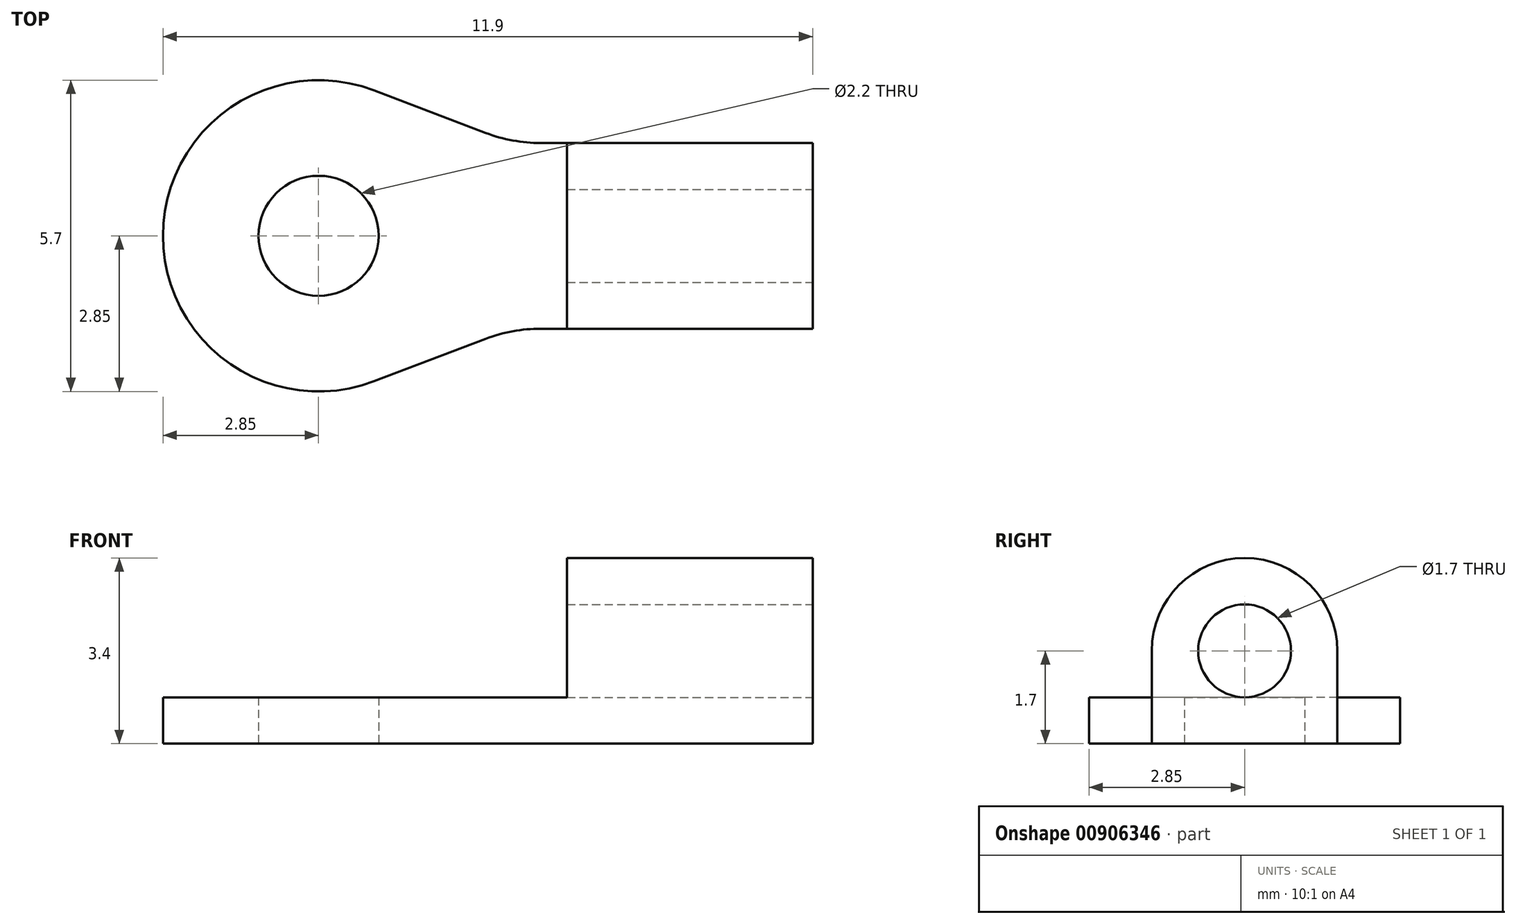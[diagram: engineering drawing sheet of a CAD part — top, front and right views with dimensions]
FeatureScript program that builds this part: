
annotation { "Feature Type Name" : "Feature", "Feature Type Description" : "" }
export const myFeature = defineFeature(function(context is Context, id is Id, definition is map)
    precondition{}
    {
        {
            var Q0;
            Q0=qCreatedBy(makeId("Top.planeOp"),FACE);
            var sketch = newSketch(context, id + "F0", { "sketchPlane" : qUnion([Q0])});
            skLineSegment(sketch, "E0.left", {"start": v(0, 2.85) * mm, "end": v(0, 2.85) * mm});
            skLineSegment(sketch, "E0.right", {"start": v(11.9, 1.15) * mm, "end": v(11.9, 4.55) * mm});
            skPoint(sketch, "E1.visualSharp", {"position": v(0, 5.7) * mm});
            skArc(sketch, "E1.filletArc", {"start": v(2.85, 5.7) * mm, "mid": v(0.83, 4.87) * mm, "end": v(0, 2.85) * mm});
            skPoint(sketch, "E2.visualSharp", {"position": v(0, 0) * mm});
            skArc(sketch, "E2.filletArc", {"start": v(0, 2.85) * mm, "mid": v(0.83, 0.83) * mm, "end": v(2.85, 0) * mm});
            skLineSegment(sketch, "E3.0", {"start": v(6.4, 1.1) * mm, "end": v(6.4, 1.15) * mm});
            skCircle(sketch, "E4", {"center": v(2.85, 2.85) * mm, "radius": 1.1 * mm});
            skArc(sketch, "E5", {"start": v(3.86, 5.51) * mm, "mid": v(0, 2.85) * mm, "end": v(3.86, 0.19) * mm});
            skLineSegment(sketch, "E6.0", {"start": v(11.9, 4.55) * mm, "end": v(6.92, 4.55) * mm});
            skLineSegment(sketch, "E7.MirrorCS", {"start": v(11.9, 1.15) * mm, "end": v(6.92, 1.15) * mm});
            skLineSegment(sketch, "E8", {"start": v(5.91, 4.74) * mm, "end": v(3.86, 5.51) * mm});
            skLineSegment(sketch, "E9", {"start": v(5.91, 0.96) * mm, "end": v(3.86, 0.19) * mm});
            skPoint(sketch, "E10.visualSharp", {"position": v(6.4, 4.55) * mm});
            skArc(sketch, "E10.filletArc", {"start": v(5.91, 4.74) * mm, "mid": v(6.4, 4.6) * mm, "end": v(6.92, 4.55) * mm});
            skPoint(sketch, "E11.visualSharp", {"position": v(6.4, 1.15) * mm});
            skArc(sketch, "E11.filletArc", {"start": v(6.92, 1.15) * mm, "mid": v(6.4, 1.1) * mm, "end": v(5.91, 0.96) * mm});
            skPoint(sketch, "E12.orphan", {"position": v(11.9, 2.85) * mm});
            skPoint(sketch, "E13.orphan", {"position": v(11.9, 5.7) * mm});
            skPoint(sketch, "E0.top.end.orphan", {"position": v(6.4, 5.7) * mm});
            skPoint(sketch, "E14.orphan", {"position": v(11.9, 0) * mm});
            skPoint(sketch, "E0.bottom.end.orphan", {"position": v(6.4, 0) * mm});
            skLineSegment(sketch, "E15.trimOffspring", {"start": v(6.4, 4.55) * mm, "end": v(6.4, 4.6) * mm});
            skPoint(sketch, "E16.end.orphan", {"position": v(6.4, 2.85) * mm});
            skSolve(sketch);
        }
        {
            var Q0;
            Q0 = qSketchRegion(id + "F0", true);
            extrude(context, id + "F1", {"entities" : qUnion([Q0]), "depth" : 0.85 * mm, "offsetDistance" : 25 * mm});
        }
        {
            var Q0;
            Q0=makeQuery(id+"F1.opExtrude","CAP_FACE",FACE,{"disambiguationData":[OSD([sQuery(id+"F0.wireOp",EDGE,"E0.right"),sQuery(id+"F0.wireOp",EDGE,"E4"),sQuery(id+"F0.wireOp",EDGE,"E5"),sQuery(id+"F0.wireOp",EDGE,"E6.0"),sQuery(id+"F0.wireOp",EDGE,"E7.MirrorCS"),sQuery(id+"F0.wireOp",EDGE,"E8"),sQuery(id+"F0.wireOp",EDGE,"E9"),sQuery(id+"F0.wireOp",EDGE,"E10.filletArc"),sQuery(id+"F0.wireOp",EDGE,"E11.filletArc")])],"isStart":false});
            var sketch = newSketch(context, id + "F2", { "sketchPlane" : qUnion([Q0])});
            skLineSegment(sketch, "E17.bottom", {"start": v(11.9, 4.55) * mm, "end": v(7.4, 4.55) * mm});
            skLineSegment(sketch, "E17.top", {"start": v(11.9, 1.15) * mm, "end": v(7.4, 1.15) * mm});
            skLineSegment(sketch, "E17.left", {"start": v(11.9, 4.55) * mm, "end": v(11.9, 1.15) * mm});
            skLineSegment(sketch, "E17.right", {"start": v(7.4, 4.55) * mm, "end": v(7.4, 1.15) * mm});
            skSolve(sketch);
        }
        {
            var Q0;
            Q0 = qSketchRegion(id + "F2", true);
            extrude(context, id + "F3", {"entities" : qUnion([Q0]), "operationType" : NewBodyOperationType.ADD, "depth" : 2.55 * mm, "offsetDistance" : 25 * mm});
        }
        {
            var Q0;
            Q0=makeQuery(id+"F3.opExtrude","CAP_EDGE",EDGE,{"disambiguationData":[OSD([sQuery(id+"F2.wireOp",EDGE,"E17.bottom")])],"isStart":false});
            var Q1;
            Q1=makeQuery(id+"F3.opExtrude","CAP_EDGE",EDGE,{"disambiguationData":[OSD([sQuery(id+"F2.wireOp",EDGE,"E17.top")])],"isStart":false});
            fillet(context, id + "F4", {"entities" : qUnion([Q0, Q1]), "radius" : 1.7 * mm, "tangentPropagation" : true, "allowEdgeOverflow" : false});
        }
        {
            var Q0;
            Q0=makeQuery(id+"F3.boolean.opBoolean","MERGE",FACE,{"derivedFrom":[makeQuery(id+"F1.opExtrude","SWEPT_FACE",FACE,{"disambiguationData":[OSD([sQuery(id+"F0.wireOp",EDGE,"E0.right")])]}),makeQuery(id+"F3.opExtrude","SWEPT_FACE",FACE,{"disambiguationData":[OSD([sQuery(id+"F2.wireOp",EDGE,"E17.left")])]})]});
            var sketch = newSketch(context, id + "F5", { "sketchPlane" : qUnion([Q0])});
            skCircle(sketch, "E18", {"center": v(2.85, 1.7) * mm, "radius": 0.85 * mm});
            skSolve(sketch);
        }
        {
            var Q0;
            Q0=makeQuery(id+"F5.imprint","IMPRINT",FACE,{"disambiguationData":[TD([[makeQuery(id+"F5.imprint","IMPRINT",EDGE,{"derivedFrom":sQuery(id+"F5.wireOp",EDGE,"E18")}),1.0]])]});
            extrude(context, id + "F6", {"entities" : qUnion([Q0]), "operationType" : NewBodyOperationType.REMOVE, "oppositeDirection" : true, "depth" : 25 * mm, "offsetDistance" : 25 * mm});
        }
    });
